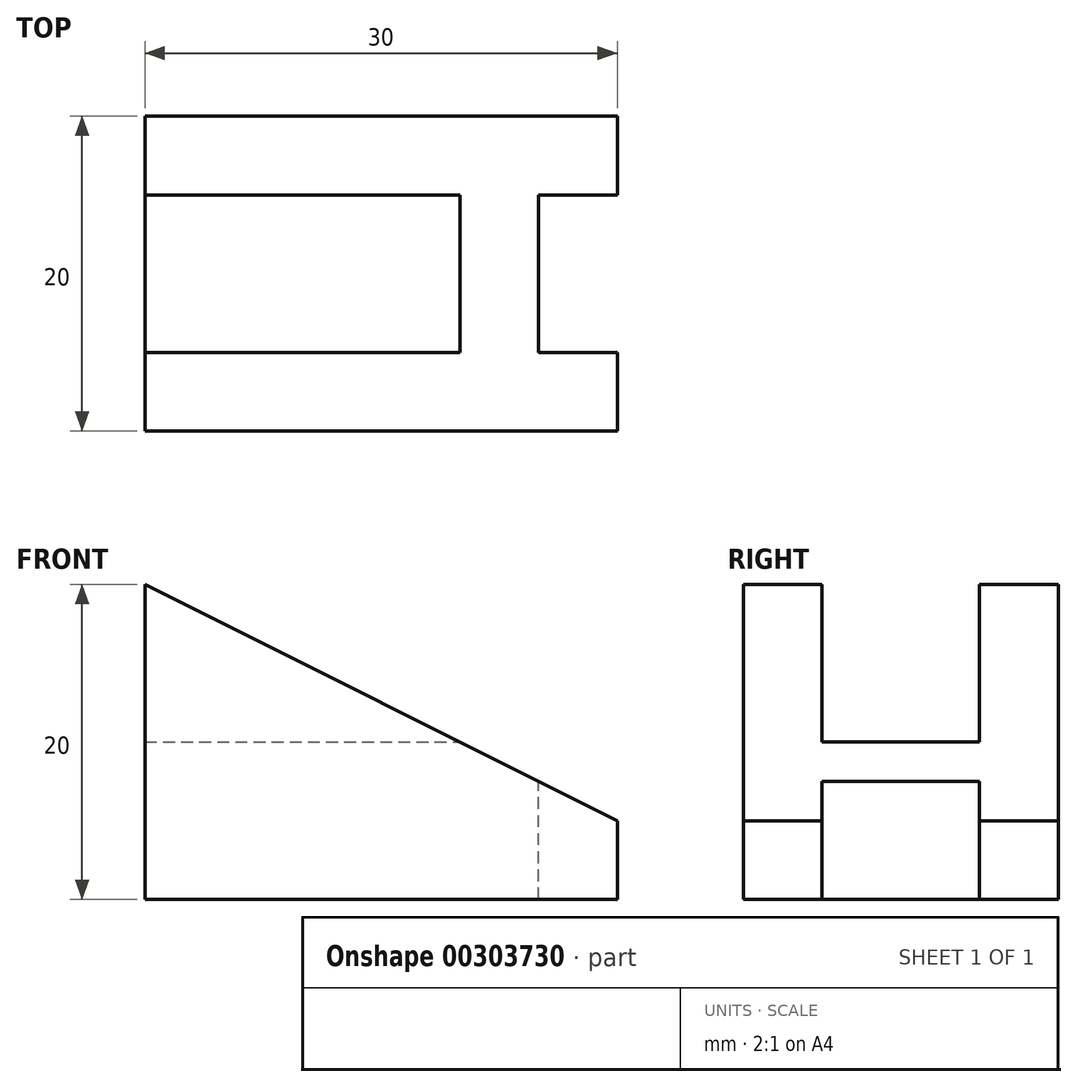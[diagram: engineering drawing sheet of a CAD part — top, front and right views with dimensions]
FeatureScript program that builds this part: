
annotation { "Feature Type Name" : "Feature", "Feature Type Description" : "" }
export const myFeature = defineFeature(function(context is Context, id is Id, definition is map)
    precondition{}
    {
        {
            var Q0;
            Q0=qCreatedBy(makeId("Front.planeOp"),FACE);
            var sketch = newSketch(context, id + "F0", { "sketchPlane" : qUnion([Q0])});
            skLineSegment(sketch, "E0", {"start": v(0, 0) * mm, "end": v(30, 0) * mm});
            skLineSegment(sketch, "E1", {"start": v(0, 20) * mm, "end": v(0, 0) * mm});
            skLineSegment(sketch, "E2", {"start": v(30, 0) * mm, "end": v(30, 5) * mm});
            skLineSegment(sketch, "E3", {"start": v(30, 5) * mm, "end": v(0, 20) * mm});
            skSolve(sketch);
        }
        {
            var Q0;
            Q0=makeQuery(id+"F0.imprint","IMPRINT",FACE,{"disambiguationData":[TD([[makeQuery(id+"F0.imprint","IMPRINT",EDGE,{"derivedFrom":sQuery(id+"F0.wireOp",EDGE,"E0")}),1.0]])]});
            extrude(context, id + "F1", {"entities" : qUnion([Q0]), "endBound" : BoundingType.SYMMETRIC, "depth" : 20 * mm});
        }
        {
            var Q0;
            Q0=qCreatedBy(makeId("Front.planeOp"),FACE);
            var sketch = newSketch(context, id + "F2", { "sketchPlane" : qUnion([Q0])});
            skLineSegment(sketch, "E4", {"start": v(0, 20) * mm, "end": v(0, 10) * mm});
            skLineSegment(sketch, "E5", {"start": v(0, 10) * mm, "end": v(20, 10) * mm});
            skLineSegment(sketch, "E6", {"start": v(20, 10) * mm, "end": v(0, 20) * mm});
            skLineSegment(sketch, "E7", {"start": v(30, 0) * mm, "end": v(25, 0) * mm});
            skLineSegment(sketch, "E8", {"start": v(25, 0) * mm, "end": v(25, 7.5) * mm});
            skLineSegment(sketch, "E9", {"start": v(30, 0) * mm, "end": v(30, 5) * mm});
            skLineSegment(sketch, "E10", {"start": v(25, 7.5) * mm, "end": v(30, 5) * mm});
            skSolve(sketch);
        }
        {
            var Q0;
            Q0 = qSketchRegion(id + "F2", true);
            extrude(context, id + "F3", {"entities" : qUnion([Q0]), "operationType" : NewBodyOperationType.REMOVE, "endBound" : BoundingType.SYMMETRIC, "oppositeDirection" : true, "depth" : 10 * mm});
        }
    });
